# Revit family: Gira_134926
name_source: partatom
category: Electrical Fixtures
revit_build: Autodesk Revit 2017 (Build: 20160225_1515(x64)
units: mm (PartAtom-declared; Revit-internal decimal feet)

## family parameters
Cut with Voids When Loaded = No
Host = Face
Maintain Annotation Orientation = Yes
Part Type = Normal
Room Calculation Point = No
Round Connector Dimension = Use Diameter
Shared = No

## types (1)
- E-Säule Licht + 3x Leereinheit 769 mm Gira Energiesäule F Alu
    Anzahl der Steckdosen = 0
    Ausführung der Oberfläche = nicht zutreffend
    Available = Yes
    Breite = 0.142 m
    Category = Licht-/Energiesäule
    Data sheet (1) = https://katalog.gira.de
    Default Elevation = 1219 mm
    Farbe = aluminium
    GTIN = 4010337349266
    Geeignet für Schutzart (IP) = IP44
    HAN = 134926
    Halogenfrei = No
    HeinzeBIM = https://bimportal.heinze.de
    Höhe = 0.769 m
    Keynote = Energiesäule_3fach
    Manufacturer URL = https://www.gira.de
    Name = E-Säule Licht + 3x Leereinheit 769 mm Gira Energiesäule F Alu
    Oberfläche = sonstige
    Region = DE
    Schaltfunktion = ohne
    Tiefe = 0.075 m
    URL = http://katalog.gira.de
    Werkstoff = sonstige
    Werkstoffgüte = sonstige

## geometry (parser evidence)
native form markers: Blend x2, Sweep x3
no freeform markers — native parametric forms only
